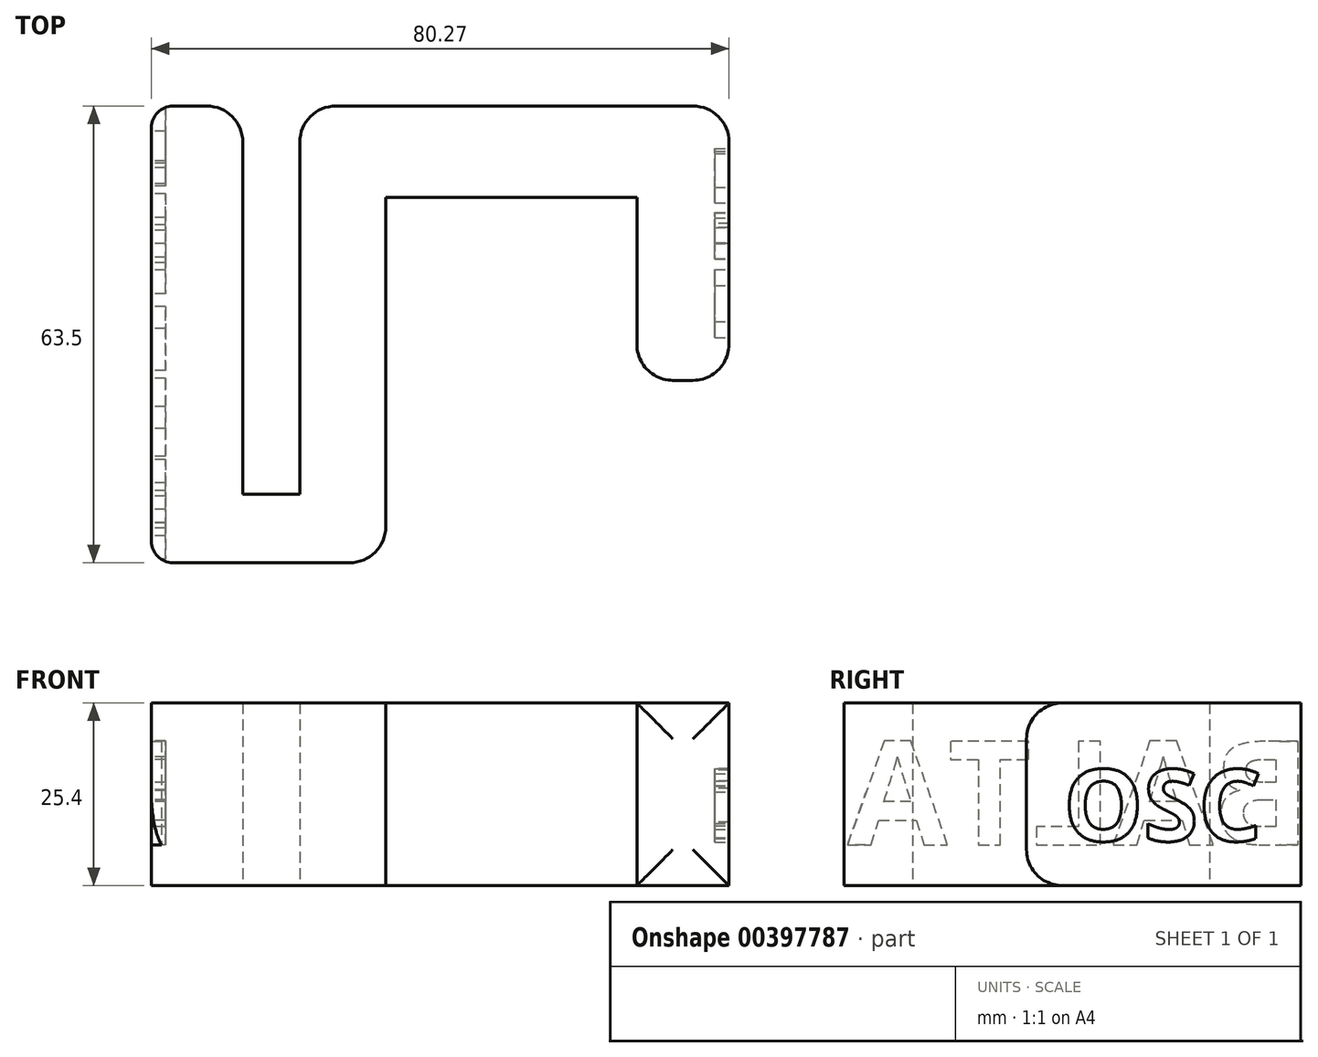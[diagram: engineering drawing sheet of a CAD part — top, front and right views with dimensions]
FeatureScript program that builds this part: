
annotation { "Feature Type Name" : "Feature", "Feature Type Description" : "" }
export const myFeature = defineFeature(function(context is Context, id is Id, definition is map)
    precondition{}
    {
        {
            var Q0;
            Q0=qCreatedBy(makeId("Top.planeOp"),FACE);
            var sketch = newSketch(context, id + "F0", { "sketchPlane" : qUnion([Q0])});
            skLineSegment(sketch, "E0", {"start": v(0, 0) * mm, "end": v(0, 63.5) * mm});
            skLineSegment(sketch, "E1", {"start": v(0, 63.5) * mm, "end": v(12.7, 63.5) * mm});
            skLineSegment(sketch, "E2", {"start": v(12.7, 63.5) * mm, "end": v(12.7, 9.53) * mm});
            skLineSegment(sketch, "E3", {"start": v(12.7, 9.53) * mm, "end": v(20.64, 9.53) * mm});
            skLineSegment(sketch, "E4", {"start": v(20.64, 9.53) * mm, "end": v(20.64, 63.5) * mm});
            skLineSegment(sketch, "E5", {"start": v(20.64, 63.5) * mm, "end": v(80.27, 63.5) * mm});
            skLineSegment(sketch, "E6", {"start": v(80.27, 63.5) * mm, "end": v(80.27, 25.35) * mm});
            skLineSegment(sketch, "E7", {"start": v(80.27, 25.35) * mm, "end": v(67.48, 25.35) * mm});
            skLineSegment(sketch, "E8", {"start": v(67.48, 25.35) * mm, "end": v(67.48, 50.8) * mm});
            skLineSegment(sketch, "E9", {"start": v(67.48, 50.8) * mm, "end": v(32.58, 50.8) * mm});
            skLineSegment(sketch, "E10", {"start": v(32.58, 50.8) * mm, "end": v(32.58, 0) * mm});
            skLineSegment(sketch, "E11", {"start": v(32.58, 0) * mm, "end": v(0, 0) * mm});
            skSolve(sketch);
        }
        {
            var Q0;
            Q0=makeQuery(id+"F0.imprint","IMPRINT",FACE,{"disambiguationData":[TD([[makeQuery(id+"F0.imprint","IMPRINT",EDGE,{"derivedFrom":sQuery(id+"F0.wireOp",EDGE,"E0")}),-1.0]])]});
            extrude(context, id + "F1", {"entities" : qUnion([Q0]), "depth" : 25.4 * mm});
        }
        {
            var Q0;
            Q0=makeQuery(id+"F1.opExtrude","CAP_EDGE",EDGE,{"disambiguationData":[OSD([sQuery(id+"F0.wireOp",EDGE,"E7")])],"isStart":false});
            var Q1;
            Q1=makeQuery(id+"F1.opExtrude","CAP_EDGE",EDGE,{"disambiguationData":[OSD([sQuery(id+"F0.wireOp",EDGE,"E7")])],"isStart":true});
            var Q2;
            Q2=makeQuery(id+"F1.opExtrude","SWEPT_EDGE",EDGE,{"disambiguationData":[OSD([sQuery(id+"F0.wireOp",EDGE,"E6"),sQuery(id+"F0.wireOp",EDGE,"E7")])]});
            var Q3;
            Q3=makeQuery(id+"F1.opExtrude","SWEPT_EDGE",EDGE,{"disambiguationData":[OSD([sQuery(id+"F0.wireOp",EDGE,"E7"),sQuery(id+"F0.wireOp",EDGE,"E8")])]});
            var Q4;
            Q4=makeQuery(id+"F1.opExtrude","SWEPT_EDGE",EDGE,{"disambiguationData":[OSD([sQuery(id+"F0.wireOp",EDGE,"E5"),sQuery(id+"F0.wireOp",EDGE,"E6")])]});
            var Q5;
            Q5=makeQuery(id+"F1.opExtrude","SWEPT_EDGE",EDGE,{"disambiguationData":[OSD([sQuery(id+"F0.wireOp",EDGE,"E10"),sQuery(id+"F0.wireOp",EDGE,"E11")])]});
            var Q6;
            Q6=makeQuery(id+"F1.opExtrude","SWEPT_EDGE",EDGE,{"disambiguationData":[OSD([sQuery(id+"F0.wireOp",EDGE,"E4"),sQuery(id+"F0.wireOp",EDGE,"E5")])]});
            var Q7;
            Q7=makeQuery(id+"F1.opExtrude","SWEPT_EDGE",EDGE,{"disambiguationData":[OSD([sQuery(id+"F0.wireOp",EDGE,"E1"),sQuery(id+"F0.wireOp",EDGE,"E2")])]});
            fillet(context, id + "F2", {"entities" : qUnion([Q0, Q1, Q2, Q3, Q4, Q5, Q6, Q7]), "radius" : 5 * mm, "tangentPropagation" : true, "allowEdgeOverflow" : false});
        }
        {
            var Q0;
            Q0=makeQuery(id+"F1.opExtrude","SWEPT_FACE",FACE,{"disambiguationData":[OSD([sQuery(id+"F0.wireOp",EDGE,"E0")])]});
            var sketch = newSketch(context, id + "F3", { "sketchPlane" : qUnion([Q0])});
            skText(sketch, "E12", { "text": "BALTA", "fontName": "OpenSans-Bold.ttf"});
            const initialGuessF3  = {"E12": [-0.06484, 0.00568, 1, 0, 0.0145]};
            skSetInitialGuess(sketch, initialGuessF3);
            skSolve(sketch);
        }
        {
            var Q0;
            Q0=qSketchRegion(id+"F3",true);
            extrude(context, id + "F4", {"entities" : qUnion([Q0]), "operationType" : NewBodyOperationType.REMOVE, "oppositeDirection" : true, "depth" : 2 * mm, "offsetDistance" : 25 * mm});
        }
        {
            var Q0;
            Q0=makeQuery(id+"F1.opExtrude","SWEPT_FACE",FACE,{"disambiguationData":[OSD([sQuery(id+"F0.wireOp",EDGE,"E6")])]});
            var sketch = newSketch(context, id + "F5", { "sketchPlane" : qUnion([Q0])});
            skText(sketch, "E13", { "text": "OSC", "fontName": "OpenSans-Bold.ttf"});
            const initialGuessF5  = {"E13": [0.0305, 0.0062, 1, 0, 0.01001]};
            skSetInitialGuess(sketch, initialGuessF5);
            skSolve(sketch);
        }
        {
            var Q0;
            Q0=qSketchRegion(id+"F5",true);
            extrude(context, id + "F6", {"entities" : qUnion([Q0]), "operationType" : NewBodyOperationType.REMOVE, "oppositeDirection" : true, "depth" : 2 * mm, "offsetDistance" : 25 * mm});
        }
        {
            var Q0;
            Q0=makeQuery(id+"F1.opExtrude","SWEPT_EDGE",EDGE,{"disambiguationData":[OSD([sQuery(id+"F0.wireOp",EDGE,"E0"),sQuery(id+"F0.wireOp",EDGE,"E11")])]});
            var Q1;
            Q1=makeQuery(id+"F1.opExtrude","SWEPT_EDGE",EDGE,{"disambiguationData":[OSD([sQuery(id+"F0.wireOp",EDGE,"E0"),sQuery(id+"F0.wireOp",EDGE,"E1")])]});
            fillet(context, id + "F7", {"entities" : qUnion([Q0, Q1]), "radius" : 3 * mm, "tangentPropagation" : true, "allowEdgeOverflow" : false});
        }
    });
